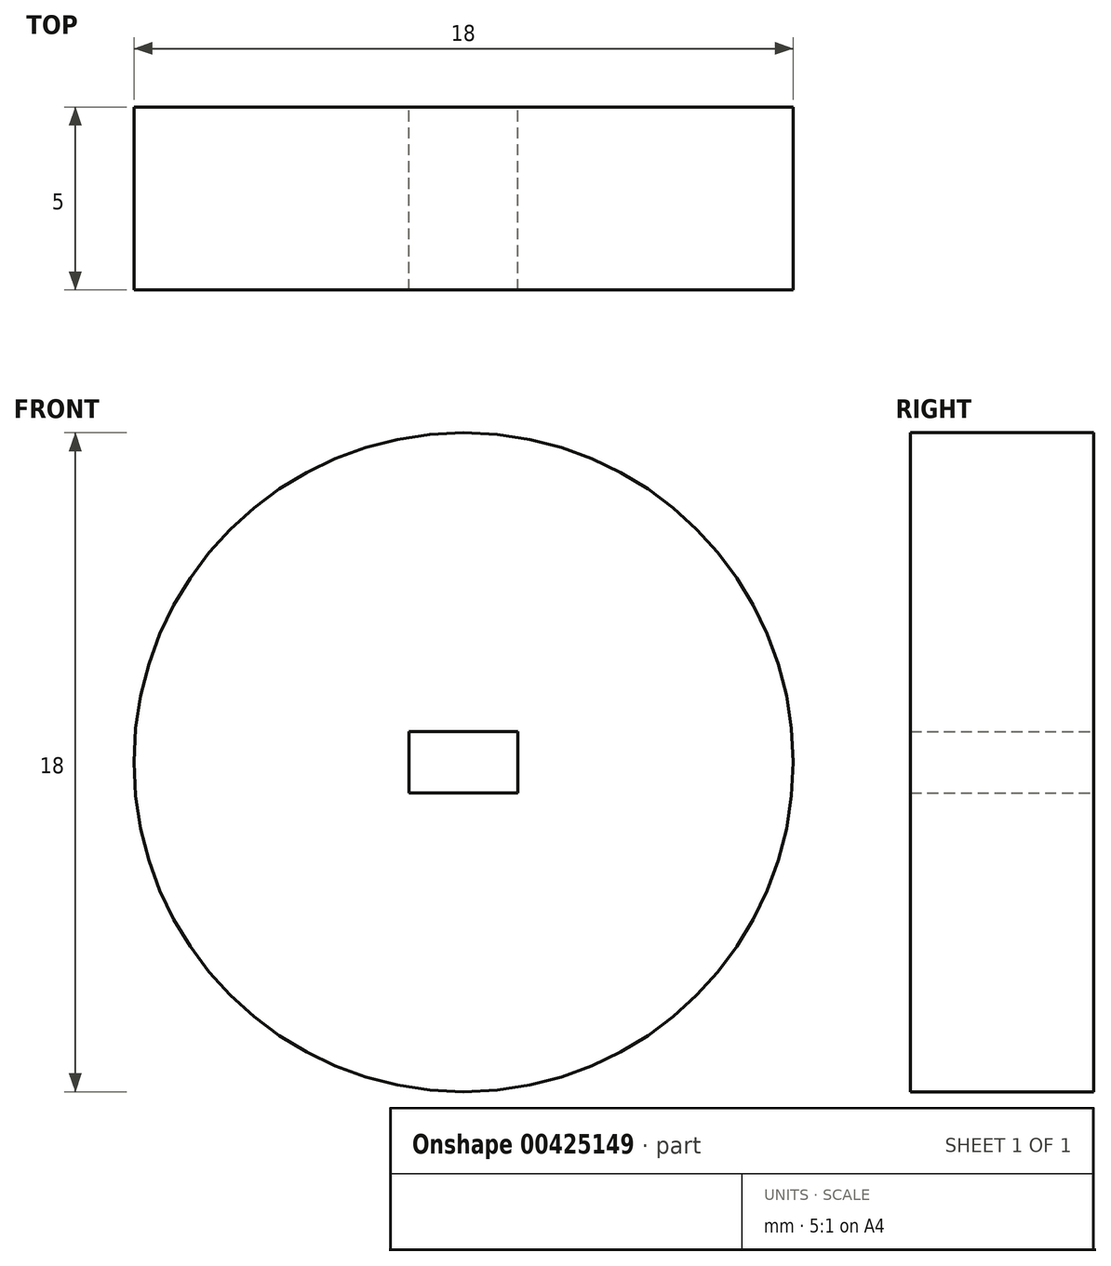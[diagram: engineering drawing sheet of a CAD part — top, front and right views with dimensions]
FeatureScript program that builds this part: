
annotation { "Feature Type Name" : "Feature", "Feature Type Description" : "" }
export const myFeature = defineFeature(function(context is Context, id is Id, definition is map)
    precondition{}
    {
        {
            var Q0;
            Q0=qCreatedBy(makeId("Front.planeOp"),FACE);
            var sketch = newSketch(context, id + "F0", { "sketchPlane" : qUnion([Q0])});
            skCircle(sketch, "E0", {"center": v(0, 0) * mm, "radius": 9 * mm});
            skSolve(sketch);
        }
        {
            var Q0;
            Q0=makeQuery(id+"F0.imprint","IMPRINT",FACE,{"disambiguationData":[TD([[makeQuery(id+"F0.imprint","IMPRINT",EDGE,{"derivedFrom":sQuery(id+"F0.wireOp",EDGE,"E0")}),1.0]])]});
            extrude(context, id + "F1", {"entities" : qUnion([Q0]), "depth" : 5 * mm});
        }
        {
            var Q0;
            Q0=qCreatedBy(makeId("Front.planeOp"),FACE);
            var sketch = newSketch(context, id + "F2", { "sketchPlane" : qUnion([Q0])});
            skLineSegment(sketch, "E1.bottom", {"start": v(1.49, 0.84) * mm, "end": v(-1.49, 0.84) * mm});
            skLineSegment(sketch, "E1.top", {"start": v(1.49, -0.84) * mm, "end": v(-1.49, -0.84) * mm});
            skLineSegment(sketch, "E1.left", {"start": v(1.49, 0.84) * mm, "end": v(1.49, -0.84) * mm});
            skLineSegment(sketch, "E1.right", {"start": v(-1.49, 0.84) * mm, "end": v(-1.49, -0.84) * mm});
            skPoint(sketch, "E1.middle", {"position": v(0, 0) * mm});
            skSolve(sketch);
        }
        {
            var Q0;
            Q0=makeQuery(id+"F2.imprint","IMPRINT",FACE,{"disambiguationData":[TD([[makeQuery(id+"F2.imprint","IMPRINT",EDGE,{"derivedFrom":sQuery(id+"F2.wireOp",EDGE,"E1.bottom")}),1.0]])]});
            extrude(context, id + "F3", {"entities" : qUnion([Q0]), "operationType" : NewBodyOperationType.REMOVE, "depth" : 9.9 * mm});
        }
    });
